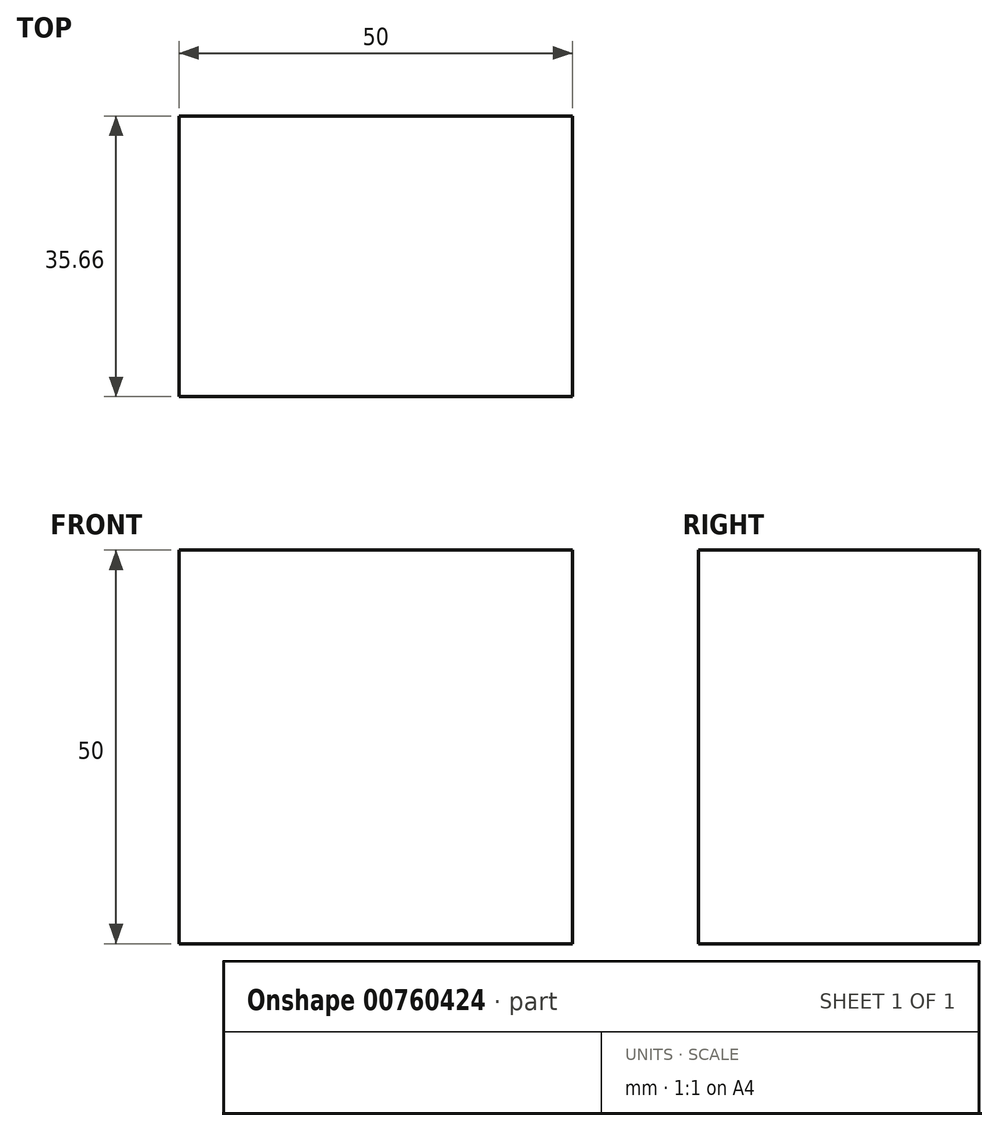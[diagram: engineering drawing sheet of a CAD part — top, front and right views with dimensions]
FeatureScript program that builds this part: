
annotation { "Feature Type Name" : "Feature", "Feature Type Description" : "" }
export const myFeature = defineFeature(function(context is Context, id is Id, definition is map)
    precondition{}
    {
        {
            var Q0;
            Q0=qCreatedBy(makeId("Front.planeOp"),FACE);
            var sketch = newSketch(context, id + "F0", { "sketchPlane" : qUnion([Q0])});
            skLineSegment(sketch, "E0.bottom", {"start": v(-25, 25) * mm, "end": v(25, 25) * mm});
            skLineSegment(sketch, "E0.top", {"start": v(-25, -25) * mm, "end": v(25, -25) * mm});
            skLineSegment(sketch, "E0.left", {"start": v(-25, 25) * mm, "end": v(-25, -25) * mm});
            skLineSegment(sketch, "E0.right", {"start": v(25, 25) * mm, "end": v(25, -25) * mm});
            skSolve(sketch);
        }
        {
            assignVariable(context, id + "F1", {"name" : "MASS", "anyValue" : 690});
        }
        {
            var Q0;
            Q0=makeQuery(id+"F0.imprint","IMPRINT",FACE,{"disambiguationData":[TD([[makeQuery(id+"F0.imprint","IMPRINT",EDGE,{"derivedFrom":sQuery(id+"F0.wireOp",EDGE,"E0.bottom")}),-1.0]])]});
            extrude(context, id + "F2", {"entities" : qUnion([Q0]), "endBound" : BoundingType.SYMMETRIC, "depth" : (getVariable(context, 'MASS') / 19.35) * mm, "offsetDistance" : 25 * mm});
        }
    });
